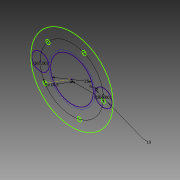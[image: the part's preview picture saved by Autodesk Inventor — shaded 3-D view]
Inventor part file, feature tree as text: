
AUTODESK INVENTOR PART (.ipt)
format: ipt  version: 2020 (Build 240168000, 168)  size: 78,336 bytes
history: native  units: mm
features: sketch x1
ambient origin geometry x8: Origin, YZ Plane, XZ Plane, XY Plane, X Axis, Y Axis, Z Axis, Center Point
feature tree (1):
  sketch  "Sketch1"  dims[d0=25.0mm d1=1.0mm d2=10.0mm d3=20.0mm d5=360.0deg d7=18.5mm d8=18.5mm d9=50.0mm d11=360.0deg]
